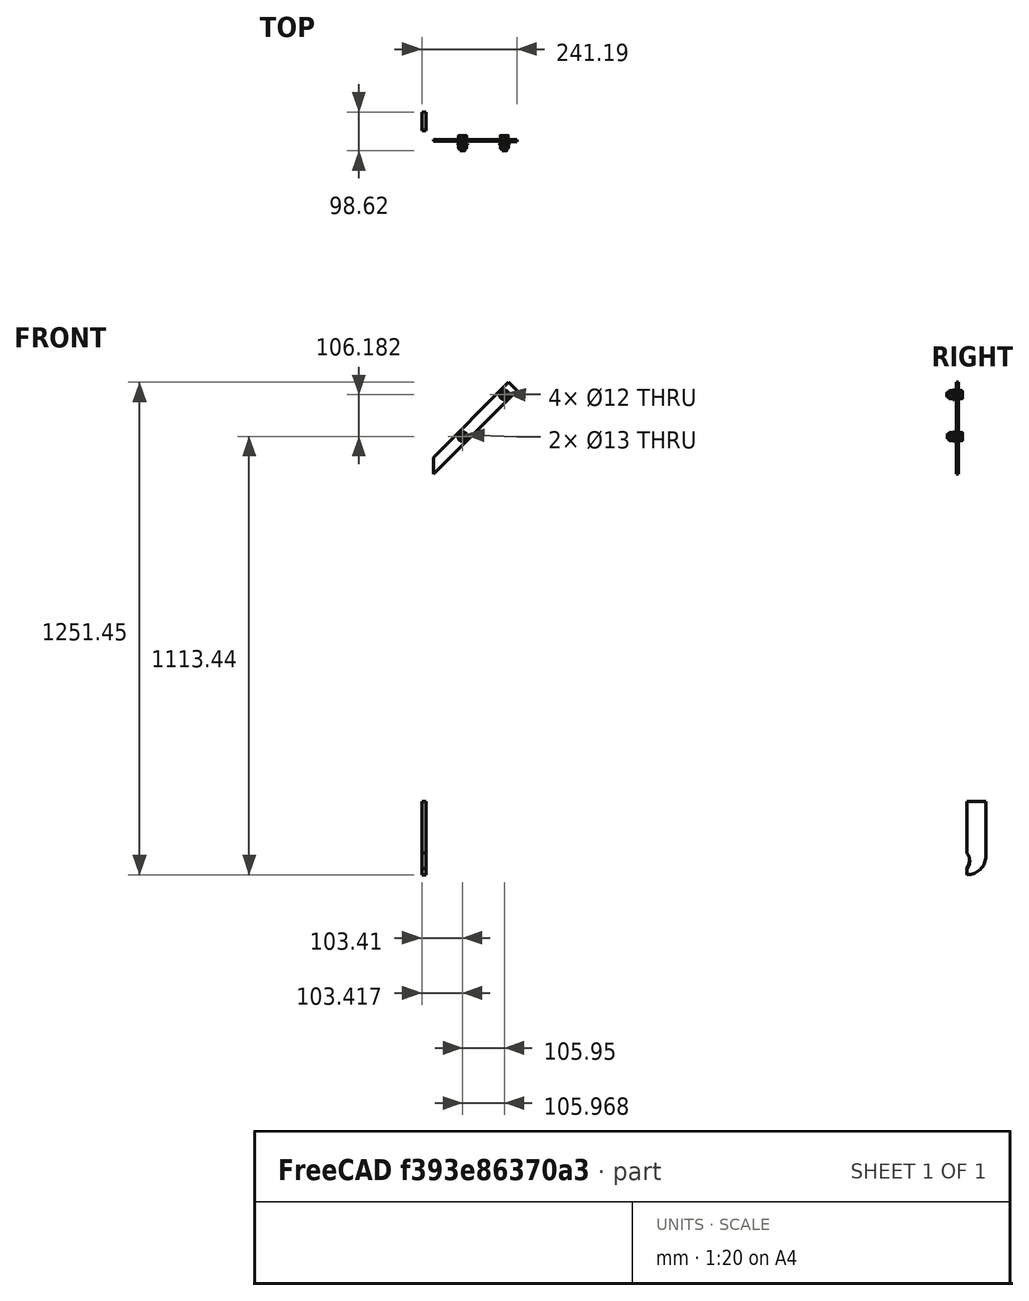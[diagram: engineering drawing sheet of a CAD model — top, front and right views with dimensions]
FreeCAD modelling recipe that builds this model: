
FCSTD DOCUMENT  (FreeCAD 0.20R29177 (Git))
Label: Tail_Assembly_BoomVane
License: All rights reserved
LicenseURL: http://en.wikipedia.org/wiki/All_rights_reserved
objects: App::Link×5, Spreadsheet::Sheet×1, Part::Mirroring×1, Part::Cylinder×1, Part::Cut×1, App::Part×1
note: 3 computed .brp shape members not serialized (recipe doc carries the construction recipe); baked Part::Feature solids carry a one-line shape summary decoded from their .brp
EXTERNAL_REF file=Boom/Tail_Boom_Support.FCStd obj=PadBody
EXTERNAL_REF file=../Master_of_Puppets.FCStd obj=HighEndStop
EXTERNAL_REF file=../Master_of_Puppets.FCStd obj=Spreadsheet
EXTERNAL_REF file=../Master_of_Puppets.FCStd obj=Tail
EXTERNAL_REF file=Vane/Tail_Vane_Bracket.FCStd obj=Part
EXTERNAL_REF file=Boom/Tail_Boom_Pipe.FCStd obj=Tube
EXTERNAL_REF file=Vane/Tail_Vane.FCStd obj=Fillet001Body
EXTERNAL_REF file=Stops/Tail_Stop_HighEnd.FCStd obj=PadBody

FEATURE [App::Link] Link001  label="Boom_Support"
  LinkPlacement = pos=(24.15,0,0) rot=(0,0,1;0.087712rad)
  LinkTransform = true
  LinkedObject = -> <external Boom/Tail_Boom_Support.FCStd>#PadBody
  Placement = pos=(24.15,0,0) rot=(0,0,1;0.087712rad)
  expr: .LinkPlacement.Base.x = Spreadsheet.TailBoomTriangularBraceX
  expr: .LinkPlacement.Base.y = Spreadsheet.TailBoomTriangularBraceY
  expr: .LinkPlacement.Base.z = Spreadsheet.TailBoomTriangularBraceZ
  expr: .LinkPlacement.Rotation.Angle = Spreadsheet.TailBoomTriangularBraceZAxisAngle
FEATURE [Spreadsheet::Sheet] Spreadsheet
  cells = A1=Inputs; A2=BoomPipeDiameter; B2(BoomPipeDiameter)==Master_of_Puppets#Spreadsheet.BoomPipeDiameter; A3=FlatMetalThickness; B3(FlatMetalThickness)==Master_of_Puppets#Spreadsheet.FlatMetalThickness; A4=BracketThickness; B4(BracketThickness)==Master_of_Puppets#Spreadsheet.BracketThickness; A5=BoomLength; B5(BoomLength)==Master_of_Puppets#Spreadsheet.BoomLength; A6=BracketLength; B6(BracketLength)==Master_of_Puppets#Spreadsheet.BracketLength; A7=BracketWidth; B7(BracketWidth)==Master_of_Puppets#Spreadsheet.BracketWidth; A8=VerticalPlaneAngle; B8(VerticalPlaneAngle)==Master_of_Puppets#Spreadsheet.VerticalPlaneAngle; A9=VaneBracketAngle; B9(VaneBracketAngle)==Master_of_Puppets#Tail.VaneBracketAngle; A10=TailBoomTriangularBraceZAxisAngle; B10(TailBoomTriangularBraceZAxisAngle)==Master_of_Puppets#Tail.TailBoomTriangularBraceZAxisAngle; A11=VaneThickness; B11(VaneThickness)==Master_of_Puppets#Spreadsheet.VaneThickness; A12=HingeOuterPipeRadius; B12(HingeOuterPipeRadius)==Master_of_Puppets#Tail.HingeOuterPipeRadius; A13=HingeOuterPipeLength; B13(HingeOuterPipeLength)==Master_of_Puppets#Tail.HingeOuterPipeLength; A14=OuterTailHingePlacement; B14(OuterTailHingePlacement)==Master_of_Puppets#Tail.OuterTailHingePlacement; A15=TailPlacement (TailBoomVaneAssembly); B15(TailPlacement)==Master_of_Puppets#HighEndStop.TailPlacement; A16=Calculated; A17=BoomPipeRadius; B17(BoomPipeRadius)==BoomPipeDiameter / 2; A18=Placement; A19=TailAssemblyBoomVane; B19=HighEndStopPlacement; A20(TailAssemblyBoomVanePlacement)==create(<<placement>>; create(<<vector>>); create(<<rotation>>; create(<<vector>>; 0; 1; 0); 90)); B20(HighEndStopPlacement)==Master_of_Puppets#HighEndStop.HighEndStopPlacement; A21=TailBoomTriangularBrace; A22=X; B22=Y; C22=Z; A23(TailBoomTriangularBraceX)==BoomPipeRadius; B23(TailBoomTriangularBraceY)=0; C23(TailBoomTriangularBraceZ)=0; A24=TopTailVaneBracket; A25=BracketWidthTriangleSide; B25=TailVaneBracketXOffset; C25=BracketLengthTriangleSide; A26(BracketWidthTriangleSide)==BracketWidth * cos(VaneBracketAngle); B26(TailVaneBracketXOffset)==BoomPipeRadius + BracketWidthTriangleSide; C26(BracketLengthTriangleSide)==BracketLength * cos(VaneBracketAngle); A27=Opposite; B27=BracketEndAdajcent; C27=BracketHypotenuse; A28(Opposite)==sin(VaneBracketAngle) * BracketLength; B28(BracketEndAdajcent)==cos(90 - VaneBracketAngle) * BracketWidth; C28(BracketHypotenuse)==BracketWidth / sin(VaneBracketAngle); A29=X; B29=Y; C29=Z; A30(TopTailVaneBracketX)==(Opposite + 2 * BoomPipeRadius - TailVaneBracketXOffset) * -1; B30(TopTailVaneBracketY)==-BracketThickness / 2; C30(TopTailVaneBracketZ)==BoomLength + BracketLengthTriangleSide + BracketEndAdajcent - BracketHypotenuse; B31=TopTailVaneBracketY Duplicated in Tail; A32=Angle; A33(TopTailVaneBracketAngle)==-VaneBracketAngle; A34=TailVane; A35=X; B35=Y; C35=Z; A36(TailVaneX)=0; B36(TailVaneY)==TopTailVaneBracketY - VaneThickness; C36(TailVaneZ)==BoomLength; A37=HingeOuterCylinder; A38(HingeOuterCylinderPlacement)==minvert(TailAssemblyBoomVanePlacement) * minvert(TailPlacement) * OuterTailHingePlacement
FEATURE [App::Link] Link004  label="Vane_Bracket_Top"
  LinkPlacement = pos=(-215.069,-2.5,1190.92) rot=(0,1,0;-0.785398rad)
  LinkTransform = true
  LinkedObject = -> <external Vane/Tail_Vane_Bracket.FCStd>#Part
  Placement = pos=(-215.069,-2.5,1190.92) rot=(0,1,0;-0.785398rad)
  expr: .LinkPlacement.Base.x = Spreadsheet.TopTailVaneBracketX
  expr: .LinkPlacement.Base.y = Spreadsheet.TopTailVaneBracketY
  expr: .LinkPlacement.Base.z = Spreadsheet.TopTailVaneBracketZ
  expr: .LinkPlacement.Rotation.Angle = Spreadsheet.TopTailVaneBracketAngle
FEATURE [App::Link] Link  label="Boom_Pipe"
  LinkedObject = -> <external Boom/Tail_Boom_Pipe.FCStd>#Tube
FEATURE [Part::Mirroring] mirror  label="Vane_Bracket_Bottom"
  Base = (0.000366211,-6.84779,1074.31)
  Normal = (1,-0.000576858,0.000545144)
  Source = -> Link004
FEATURE [App::Link] Link005  label="Vane"
  LinkPlacement = pos=(0,-8.5,1000) rot=(-0.57735,-0.57735,-0.57735;2.0944rad)
  LinkedObject = -> <external Vane/Tail_Vane.FCStd>#Fillet001Body
  Placement = pos=(0,-8.5,1000) rot=(-0.57735,-0.57735,-0.57735;2.0944rad)
  expr: .Placement.Base.x = Spreadsheet.TailVaneX
  expr: .Placement.Base.y = Spreadsheet.TailVaneY
  expr: .Placement.Base.z = Spreadsheet.TailVaneZ
FEATURE [Part::Cylinder] Cylinder  label="Hinge_Outer_Cylinder"
  Angle = 360
  AttacherType = Attacher::AttachEngine3D
  FirstAngle = 0
  Height = 126.076
  Placement = pos=(74.8689,7.40405,-49.5225) rot=(0.183254,-0.974655,-0.128316;1.24596rad)
  Radius = 30.15
  SecondAngle = 0
  expr: Height = Spreadsheet.HingeOuterPipeLength
  expr: Placement = Spreadsheet.HingeOuterCylinderPlacement
  expr: Radius = Spreadsheet.HingeOuterPipeRadius
FEATURE [App::Link] Link002  label="Stop_HighEnd_Link"
  LinkPlacement = pos=(5,24.15,0) rot=(0,1,0;-1.5708rad)
  LinkedObject = -> <external Stops/Tail_Stop_HighEnd.FCStd>#PadBody
  Placement = pos=(5,24.15,0) rot=(0,1,0;-1.5708rad)
  expr: Placement = Spreadsheet.HighEndStopPlacement
FEATURE [Part::Cut] Cut  label="Tail_Stop_HighEnd"
  Base = -> Link002
  Openafpm_Flat = true
  Tool = -> Cylinder
FEATURE [App::Part] Part001  label="Tail_Assembly_BoomVane"
  Group = -> [Link,Link001,Link004,mirror,Link005,Link002,Cylinder,Cut]
  Origin = -> Origin001
  Placement = pos=(0,0,0) rot=(0,1,0;1.5708rad)

RESOLVED EXTERNAL PARTS (link-assembly join: the EXTERNAL_REF files above that resolve inside this repo's crawl, each included once):
---- part ../Master_of_Puppets.FCStd = doc fcstd_6404554055c4 (61625 chars; too large to inline — full recipe in that document) ----
---- part Boom/Tail_Boom_Support.FCStd = doc fcstd_6b65ddd8a587 ----
FCSTD DOCUMENT  (FreeCAD 0.19R24366 (Git))
Label: Tail_Boom_Support
License: All rights reserved
LicenseURL: http://en.wikipedia.org/wiki/All_rights_reserved
objects: Sketcher::SketchObject×1, PartDesign::Pad×1, Spreadsheet::Sheet×1, PartDesign::Body×1
note: 4 computed .brp shape members not serialized (recipe doc carries the construction recipe); baked Part::Feature solids carry a one-line shape summary decoded from their .brp
EXTERNAL_REF file=../../Master_of_Puppets.FCStd obj=Spreadsheet
EXTERNAL_REF file=../../Master_of_Puppets.FCStd obj=Tail

FEATURE [Sketcher::SketchObject] Sketch
  FullyConstrained = true
  MapMode = 5
  Support = -> [XY_Plane001]
  expr: Constraints[17] = Spreadsheet.SupportLength
  expr: Constraints[2] = Spreadsheet.TailBoomTriangularBraceLength
  expr: Constraints[16] = Spreadsheet.SupportWidth
  expr: Constraints[7] = Spreadsheet.TriangularAngle
  expr: Constraints[4] = Spreadsheet.TailBoomTriangularBraceWidth
  sketch-geometry (7):
    g0: LineSegment StartX=333.333 StartY=0 StartZ=0 EndX=-26.8829 EndY=-73.86 EndZ=0
    g1: LineSegment StartX=0 StartY=0 StartZ=0 EndX=333.333 EndY=0 EndZ=0
    g2: LineSegment StartX=-26.8829 StartY=-73.86 StartZ=0 EndX=0 EndY=0 EndZ=0
    g3: LineSegment StartX=-26.8829 StartY=-73.86 StartZ=0 EndX=333.333 EndY=0 EndZ=0
    g4: LineSegment StartX=-26.8829 StartY=-73.86 StartZ=0 EndX=1.14859e-11 EndY=1.64988e-11 EndZ=0
    g5: LineSegment StartX=1.14859e-11 StartY=1.64988e-11 StartZ=0 EndX=1.6e-14 EndY=0 EndZ=0
    g6: LineSegment StartX=1.6e-14 StartY=0 StartZ=0 EndX=333.333 EndY=0 EndZ=0
  constraints (18):
    c: PointOnObject(g0,g-1)
    c: Coincident(g0,g1)
    c: Distance(g1,g0) = 333.333
    c: Coincident(g2,g0)
    c: Distance(g2,g0) = 78.6002
    c: Coincident(g1,g2)
    c: Coincident(g1,g-1)
    c: Angle(g2,g1) = 1.91986
    c: Coincident(g3,g0)
    c: Coincident(g3,g0)
    c: Coincident(g4,g3)
    c: PointOnObject(g4,g2)
    c: Coincident(g5,g4)
    c: PointOnObject(g5,g1)
    c: Coincident(g6,g5)
    c: Coincident(g6,g3)
    c: Distance(g4,g3) = 78.6002
    c: Distance(g5,g3) = 333.333
FEATURE [PartDesign::Pad] Pad
  AllowMultiFace = false
  Direction = (1,1,1)
  Length = 10
  Length2 = 100
  Profile = -> Sketch
  Type = 0
  expr: Length = Spreadsheet.FlatMetalThickness
FEATURE [Spreadsheet::Sheet] Spreadsheet
  cells = A1=Inputs; A2=CalculatedWindTurbineShape; B2(CalculatedWindTurbineShape)==Master_of_Puppets#Spreadsheet.CalculatedWindTurbineShape; D2=a; E2(a)==TailBoomTriangularBraceWidth; A3=VerticalPlaneAngle; B3(VerticalPlaneAngle)==Master_of_Puppets#Spreadsheet.VerticalPlaneAngle; D3=b; E3(b)==TailBoomTriangularBraceLength; A4=FlatMetalThickness; B4(FlatMetalThickness)==Master_of_Puppets#Spreadsheet.FlatMetalThickness; D4=c; E4(c)==sqrt(a ^ 2 + b ^ 2 - 2 * a * b * cos(TriangularAngle)); F4=Law of Cosines; A5=TailBoomTriangularBraceWidth; B5(TailBoomTriangularBraceWidth)==Master_of_Puppets#Tail.TailBoomTriangularBraceWidth; D5=AngleA; E5(AngleA)==acos((a ^ 2 + c ^ 2 - b ^ 2) / (2 * a * c)); F5=Law of Cosines; A6=TailBoomTriangularBraceLength; B6(TailBoomTriangularBraceLength)==Master_of_Puppets#Tail.TailBoomTriangularBraceLength; D6=AngleB; E6(AngleB)==acos((b ^ 2 + c ^ 2 - a ^ 2) / (2 * b * c)); F6=Law of Cosines; A7=Calculated; D7=WidthOfFlatBar; E7(WidthOfFlatBar)=100; A8=TriangularAngle; B8(TriangularAngle)==90 + VerticalPlaneAngle; D8=x; E8(x)==WidthOfFlatBar / sin(AngleB); A9=Y; B9(Y)==FlatMetalThickness / 2; D9=y; E9(y)==WidthOfFlatBar / sin(AngleA); A10=SupportWidth; B10(SupportWidth)==CalculatedWindTurbineShape == <<T>> ? TailBoomTriangularBraceWidth : y; A11=SupportLength; B11(SupportLength)==CalculatedWindTurbineShape == <<T>> ? TailBoomTriangularBraceLength : x
FEATURE [PartDesign::Body] PadBody  label="Tail_Boom_Support"
  Group = -> [Sketch,Pad]
  Openafpm_Flat = true
  Origin = -> Origin001
  Placement = pos=(0,5,0) rot=(0.57735,-0.57735,0.57735;2.0944rad)
  Tip = -> Pad
  expr: .Placement.Base.y = Spreadsheet.Y
---- part Stops/Tail_Stop_HighEnd.FCStd = doc fcstd_737cbc09fbdb ----
FCSTD DOCUMENT  (FreeCAD 0.21R33771 (Git))
Label: Tail_Stop_HighEnd
License: All rights reserved
LicenseURL: http://en.wikipedia.org/wiki/All_rights_reserved
objects: Sketcher::SketchObject×1, PartDesign::Pad×1, Spreadsheet::Sheet×1, PartDesign::Body×1
note: 4 computed .brp shape members not serialized (recipe doc carries the construction recipe); baked Part::Feature solids carry a one-line shape summary decoded from their .brp
EXTERNAL_REF file=../../Master_of_Puppets.FCStd obj=HighEndStop
EXTERNAL_REF file=../../Master_of_Puppets.FCStd obj=Spreadsheet
EXTERNAL_REF file=../../Master_of_Puppets.FCStd obj=Tail

FEATURE [Sketcher::SketchObject] Sketch
  FullyConstrained = true
  MapMode = 5
  Support = -> [XY_Plane001]
  expr: Constraints[14] = Spreadsheet.HingeOuterPipeRadius
  expr: Constraints[16] = Spreadsheet.HingeOuterPipeDiameter
  expr: Constraints[1] = Spreadsheet.HighEndStopWidth
  expr: Constraints[3] = Spreadsheet.HighEndStopLength
  expr: Constraints[8] = Spreadsheet.HighEndStopWidthExtensionToLowEndStop
  sketch-geometry (7):
    g0: LineSegment StartX=223.325 StartY=0 StartZ=0 EndX=223.325 EndY=118.216 EndZ=0
    g1: ArcOfCircle CenterX=16.6164 CenterY=0 CenterZ=0 NormalX=0 NormalY=0 NormalZ=1 AngleXU=0 Radius=118.216 StartAngle=1.5708 EndAngle=3.14159
    g2: LineSegment StartX=16.6164 StartY=118.216 StartZ=0 EndX=223.325 EndY=118.216 EndZ=0
    g3: LineSegment StartX=-101.6 StartY=1.45e-14 StartZ=0 EndX=-101.6 EndY=-4.64258 EndZ=0
    g4: LineSegment StartX=-101.6 StartY=-4.64258 StartZ=0 EndX=-50.8 EndY=-4.64258 EndZ=0
    g5: LineSegment StartX=-50.8 StartY=-4.64258 StartZ=0 EndX=-50.8 EndY=0 EndZ=0
    g6: LineSegment StartX=223.325 StartY=0 StartZ=0 EndX=-50.8 EndY=0 EndZ=0
  constraints (22):
    c: Vertical(g0)
    c: DistanceY(g0,g0) = 118.216
    c: PointOnObject(g1,g-1)
    c: DistanceX(g-1,g0) = 223.325
    c: Coincident(g2,g1)
    c: Coincident(g2,g0)
    c: Vertical(g3)
    c: Coincident(g3,g4)
    c: DistanceY(g4,g1) = 4.64258
    c: Coincident(g3,g1)
    c: Horizontal(g2)
    c: Coincident(g5,g4)
    c: PointOnObject(g5,g-1)
    c: Vertical(g5)
    c: DistanceX(g4,g4) = 50.8
    c: Horizontal(g4)
    c: DistanceX(g1,g-1) = 101.6
    c: Vertical(g1,g1)
    c: Coincident(g6,g0)
    c: Coincident(g6,g5)
    c: Horizontal(g6)
    c: PointOnObject(g1,g6)
FEATURE [PartDesign::Pad] Pad
  AllowMultiFace = false
  Direction = (0,0,1)
  Length = 10
  Length2 = 100
  Profile = -> Sketch
  Type = 0
  expr: Length = Spreadsheet.FlatMetalThickness
FEATURE [Spreadsheet::Sheet] Spreadsheet
  cells = A1='Inputs; A2='FlatMetalThickness; B2(FlatMetalThickness)==Master_of_Puppets#Spreadsheet.FlatMetalThickness; A3='HingeOuterPipeRadius; B3(HingeOuterPipeRadius)==Master_of_Puppets#Tail.HingeOuterPipeRadius; A4='HighEndStopWidth; B4(HighEndStopWidth)==Master_of_Puppets#HighEndStop.HighEndStopWidth; A5='HighEndStopLength; B5(HighEndStopLength)==Master_of_Puppets#HighEndStop.HighEndStopLength; A6='HighEndStopWidthExtensionToLowEndStop; B6(HighEndStopWidthExtensionToLowEndStop)==Master_of_Puppets#HighEndStop.HighEndStopWidthExtensionToLowEndStop; A7='Calculated; A8='HingeOuterPipeDiameter; B8(HingeOuterPipeDiameter)==HingeOuterPipeRadius * 2; C8='Distance stop extends towards the outer tail hinge
FEATURE [PartDesign::Body] PadBody  label="Tail_Stop_HighEnd"
  Group = -> [Sketch,Pad]
  Origin = -> Origin001
  Tip = -> Pad
---- part Vane/Tail_Vane.FCStd = doc fcstd_911bd00fbed7 ----
FCSTD DOCUMENT  (FreeCAD 1.0R39109 (Git))
Label: Tail_Vane
License: All rights reserved
LicenseURL: http://en.wikipedia.org/wiki/All_rights_reserved
objects: Sketcher::SketchObject×2, PartDesign::Pad×1, Spreadsheet::Sheet×1, PartDesign::Plane×1, PartDesign::Pocket×1, PartDesign::Mirrored×1, PartDesign::Fillet×1, PartDesign::Body×1
note: 17 computed .brp shape members not serialized (recipe doc carries the construction recipe); baked Part::Feature solids carry a one-line shape summary decoded from their .brp
EXTERNAL_REF file=../../Master_of_Puppets.FCStd obj=Alternator
EXTERNAL_REF file=../../Master_of_Puppets.FCStd obj=Spreadsheet
EXTERNAL_REF file=../../Master_of_Puppets.FCStd obj=Tail

FEATURE [Sketcher::SketchObject] Sketch
  ArcFitTolerance = 0
  AttachmentSupport = -> [XY_Plane001]
  FullyConstrained = true
  MakeInternals = false
  MapMode = 5
  expr: Constraints[16] = Spreadsheet.VaneWidth
  expr: Constraints[17] = Spreadsheet.VaneLength
  expr: Constraints[18] = Spreadsheet.LengthSmallSide
  expr: Constraints[19] = Spreadsheet.WidthSmall
  sketch-geometry (7):
    g0: LineSegment StartX=0 StartY=94.8607 StartZ=0 EndX=0 EndY=0 EndZ=0
    g1: LineSegment StartX=0 StartY=0 StartZ=0 EndX=0 EndY=-94.8607 EndZ=0
    g2: LineSegment StartX=0 StartY=-94.8607 StartZ=0 EndX=427.594 EndY=-1000 EndZ=0
    g3: LineSegment StartX=427.594 StartY=-1000 StartZ=0 EndX=900 EndY=-1000 EndZ=0
    g4: LineSegment StartX=900 StartY=-1000 StartZ=0 EndX=900 EndY=1000 EndZ=0
    g5: LineSegment StartX=900 StartY=1000 StartZ=0 EndX=427.594 EndY=1000 EndZ=0
    g6: LineSegment StartX=427.594 StartY=1000 StartZ=0 EndX=0 EndY=94.8607 EndZ=0
  constraints (20):
    c: PointOnObject(g0,g-2)
    c: Coincident(g0,g-1)
    c: Coincident(g-1,g1)
    c: PointOnObject(g1,g-2)
    c: Coincident(g1,g2)
    c: Coincident(g2,g3)
    c: Horizontal(g3)
    c: Coincident(g3,g4)
    c: Vertical(g4)
    c: Coincident(g4,g5)
    c: Horizontal(g5)
    c: Coincident(g5,g6)
    c: Coincident(g6,g0)
    c: Equal(g6,g2)
    c: Equal(g5,g3)
    c: Equal(g0,g1)
    c: DistanceX(g-1,g4) = 900
    c: DistanceY(g4,g4) = 2000
    c: DistanceY(g1,g1) = 94.8607
    c: DistanceX(g5,g5) = 472.406
FEATURE [PartDesign::Pad] Pad
  AllowMultiFace = false
  Direction = (0,0,1)
  Length = 9
  Length2 = 100
  Profile = -> Sketch
  Suppressed = false
  Type = 0
  expr: Length = Spreadsheet.VaneThickness
FEATURE [Spreadsheet::Sheet] Spreadsheet
  cells = A1='Inputs; A2='RotorRadius; B2(RotorRadius)==Master_of_Puppets#Spreadsheet.RotorDiskRadius; A3='BoomPipeDiameter; B3(BoomPipeDiameter)==Master_of_Puppets#Spreadsheet.BoomPipeDiameter; A4='HolesRadius; B4(HolesRadius)==Master_of_Puppets#Alternator.HolesRadius; A5='BracketLength; B5(BracketLength)==Master_of_Puppets#Spreadsheet.BracketLength; A6='BracketWidth; B6(BracketWidth)==Master_of_Puppets#Spreadsheet.BracketWidth; A7='VaneLength; B7(VaneLength)==Master_of_Puppets#Spreadsheet.VaneLength; A8='VaneWidth; B8(VaneWidth)==Master_of_Puppets#Spreadsheet.VaneWidth; A9='VaneThickness; B9(VaneThickness)==Master_of_Puppets#Spreadsheet.VaneThickness; A10='DistanceToFirstHole; B10(DistanceToFirstHole)==Master_of_Puppets#Tail.DistanceToFirstHole; A11='DistanceBetweenHoles; B11(DistanceBetweenHoles)==Master_of_Puppets#Tail.DistanceBetweenHoles; A12='VaneBracketAngle; B12(VaneBracketAngle)==Master_of_Puppets#Tail.VaneBracketAngle; A13='Calculated; A14='BoomPipeRadius; B14(BoomPipeRadius)==BoomPipeDiameter / 2; A15='Y_Holes; B15(Y_Holes)==BracketWidth / 2; C15='Duplicated in TailVaneBracket; A16='WidthAngleBracket; B16(WidthAngleBracket)==BracketWidth / cos(VaneBracketAngle); A17='HalfWidthAngleBracket; B17(HalfWidthAngleBracket)==WidthAngleBracket / 2; A18='LengthSmallSide; B18(LengthSmallSide)==tan(VaneBracketAngle) * WidthAngleBracket + BoomPipeRadius; A19='WidthSmall; B19(WidthSmall)==0.5 * VaneWidth / (1 - LengthSmallSide / VaneLength); A20='DistanceToFirstHoleFromMiddlePoint; B20(DistanceToFirstHoleFromMiddlePoint)==BracketLength - Y_Holes - DistanceToFirstHole
FEATURE [PartDesign::Plane] DatumPlane
  Length = 60
  MapMode = 2
  Placement = pos=(0,0,9) rot=(0,0,1;0rad)
  ResizeMode = 0
  Width = 60
  expr: .Placement.Base.z = Spreadsheet.VaneThickness
FEATURE [Sketcher::SketchObject] Sketch001  label="HolesSketch"
  ArcFitTolerance = 0
  AttachmentSupport = -> [DatumPlane]
  FullyConstrained = true
  MakeInternals = false
  MapMode = 5
  Placement = pos=(0,0,9) rot=(0,0,1;0rad)
  expr: Constraints[0] = Spreadsheet.BoomPipeRadius
  expr: Constraints[11] = Spreadsheet.BracketLength
  expr: Constraints[13] = Spreadsheet.DistanceToFirstHoleFromMiddlePoint
  expr: Constraints[18] = Spreadsheet.WidthAngleBracket / 2
  expr: Constraints[2] = Spreadsheet.Y_Holes
  expr: Constraints[4] = Spreadsheet.DistanceBetweenHoles
  expr: Constraints[6] = Spreadsheet.HolesRadius
  expr: Constraints[7] = Spreadsheet.HolesRadius
  expr: Constraints[8] = Spreadsheet.WidthAngleBracket
  sketch-geometry (7):
    g0: LineSegment [constr] StartX=353.553 StartY=-448.414 StartZ=0 EndX=388.909 EndY=-413.059 EndZ=0
    g1: LineSegment [constr] StartX=371.231 StartY=-430.736 StartZ=0 EndX=-35.3553 EndY=-24.15 EndZ=0
    g2: Circle CenterX=328.805 CenterY=-388.31 CenterZ=0 NormalX=0 NormalY=0 NormalZ=1 AngleXU=0 Radius=7
    g3: Circle CenterX=116.673 CenterY=-176.178 CenterZ=0 NormalX=0 NormalY=0 NormalZ=1 AngleXU=0 Radius=7
    g4: LineSegment [constr] StartX=388.909 StartY=-413.059 StartZ=0 EndX=0 EndY=-24.15 EndZ=0
    g5: LineSegment [constr] StartX=353.553 StartY=-448.414 StartZ=0 EndX=-70.7107 EndY=-24.15 EndZ=0
    g6: LineSegment [constr] StartX=-70.7107 StartY=-24.15 StartZ=0 EndX=0 EndY=-24.15 EndZ=0
  constraints (22):
    c: DistanceY(g4,g-1) = 24.15
    c: PointOnObject(g1,g0)
    c: Distance(g1,g0) = 25
    c: PointOnObject(g3,g1)
    c: Distance(g2,g3) = 300
    c: Angle(g1) = 2.35619
    c: Radius(g3) = 7
    c: Radius(g2) = 7
    c: Distance(g6,g4) = 70.7107
    c: Coincident(g4,g0)
    c: Coincident(g5,g0)
    c: Distance(g6,g0) = 600
    c: PointOnObject(g2,g1)
    c: Distance(g2,g1) = 515
    c: Perpendicular(g0,g1)
    c: PointOnObject(g4,g-2)
    c: Horizontal(g6)
    c: PointOnObject(g1,g6)
    c: Distance(g4,g1) = 35.3553
    c: Coincident(g5,g6)
    c: Coincident(g4,g6)
    c: Perpendicular(g5,g0)
FEATURE [PartDesign::Pocket] Pocket
  BaseFeature = -> Pad
  Direction = (0,0,-1)
  Length = 9
  Length2 = 100
  Profile = -> Sketch001
  Suppressed = false
  Type = 0
  expr: Length = Spreadsheet.VaneThickness
FEATURE [PartDesign::Mirrored] Mirrored
  BaseFeature = -> Pocket
  MirrorPlane = -> Sketch001 [H_Axis]
  Originals = -> [Pocket]
  Suppressed = false
  TransformMode = 0
FEATURE [PartDesign::Fillet] Fillet
  Base = -> Mirrored [Edge1,Edge8,Edge28,Edge29,Edge27,Edge5]
  BaseFeature = -> Mirrored
  Radius = 50
  SupportTransform = false
  Suppressed = false
  UseAllEdges = false
FEATURE [PartDesign::Body] Fillet001Body  label="Tail_Vane"
  AllowCompound = false
  Group = -> [Sketch,Pad,DatumPlane,Sketch001,Pocket,Mirrored,Fillet]
  Openafpm_Flat = true
  Origin = -> Origin001
  Placement = pos=(0,0,8) rot=(0,0,1;0rad)
  Tip = -> Fillet
---- part Vane/Tail_Vane_Bracket.FCStd = doc fcstd_d393650c2bc9 ----
FCSTD DOCUMENT  (FreeCAD 0.21R33771 (Git))
Label: Tail_Vane_Bracket
License: All rights reserved
LicenseURL: http://en.wikipedia.org/wiki/All_rights_reserved
objects: App::Link×4, Sketcher::SketchObject×2, App::Part×2, PartDesign::Pad×1, PartDesign::Pocket×1, Spreadsheet::Sheet×1, PartDesign::Body×1
note: 7 computed .brp shape members not serialized (recipe doc carries the construction recipe); baked Part::Feature solids carry a one-line shape summary decoded from their .brp
EXTERNAL_REF file=../../Master_of_Puppets.FCStd obj=Alternator
EXTERNAL_REF file=../../Master_of_Puppets.FCStd obj=Fastener
EXTERNAL_REF file=../../Master_of_Puppets.FCStd obj=Spreadsheet
EXTERNAL_REF file=../../Master_of_Puppets.FCStd obj=Tail
EXTERNAL_REF file=../../Fasteners/Fastener_Bolt_Tail_Vane.FCStd obj=Body
EXTERNAL_REF file=../../Fasteners/Fastener_HexNut.FCStd obj=Body
EXTERNAL_REF file=../../Fasteners/Fastener_Washer_Wide.FCStd obj=Tube

FEATURE [Sketcher::SketchObject] Sketch
  FullyConstrained = true
  MapMode = 5
  Support = -> [XY_Plane001]
  expr: Constraints[10] = Spreadsheet.Length
  expr: Constraints[7] = Spreadsheet.VaneBracketAngle
  expr: Constraints[8] = Spreadsheet.Width
  sketch-geometry (4):
    g0: LineSegment StartX=300 StartY=30 StartZ=0 EndX=0 EndY=30 EndZ=0
    g1: LineSegment StartX=0 StartY=30 StartZ=0 EndX=0 EndY=0 EndZ=0
    g2: LineSegment StartX=0 StartY=0 StartZ=0 EndX=270 EndY=0 EndZ=0
    g3: LineSegment StartX=270 StartY=0 StartZ=0 EndX=300 EndY=30 EndZ=0
  constraints (11):
    c: Coincident(g0,g1)
    c: Horizontal(g0)
    c: Vertical(g1)
    c: Coincident(g-1,g2)
    c: Horizontal(g2)
    c: Coincident(g2,g3)
    c: Coincident(g3,g0)
    c: Angle(g0,g3) = 0.785398
    c: DistanceY(g1,g1) = 30
    c: Coincident(g1,g-1)
    c: Distance(g0) = 300
FEATURE [PartDesign::Pad] Pad
  AllowMultiFace = false
  Direction = (0,0,1)
  Length = 5
  Length2 = 100
  Profile = -> Sketch
  Type = 0
  expr: Length = Spreadsheet.BracketThickness
FEATURE [Sketcher::SketchObject] Sketch001
  FullyConstrained = true
  MapMode = 5
  Placement = pos=(0,0,5) rot=(0,0,1;0rad)
  Support = -> [Pad]
  expr: Constraints[10] = Spreadsheet.DistanceBetweenHoles
  expr: Constraints[7] = Spreadsheet.Y_Holes
  expr: Constraints[8] = Spreadsheet.HolesRadius
  expr: Constraints[9] = Spreadsheet.DistanceToFirstHole
  sketch-geometry (4):
    g0: Circle CenterX=30 CenterY=15 CenterZ=0 NormalX=0 NormalY=0 NormalZ=1 AngleXU=0 Radius=6
    g1: Circle CenterX=180 CenterY=15 CenterZ=0 NormalX=0 NormalY=0 NormalZ=1 AngleXU=0 Radius=6
    g2: LineSegment StartX=0 StartY=15 StartZ=0 EndX=30 EndY=15 EndZ=0
    g3: LineSegment StartX=30 StartY=15 StartZ=0 EndX=180 EndY=15 EndZ=0
  constraints (11):
    c: Equal(g1,g0)
    c: PointOnObject(g2,g-2)
    c: Coincident(g2,g0)
    c: Horizontal(g2)
    c: Coincident(g2,g3)
    c: Coincident(g3,g1)
    c: Horizontal(g3)
    c: Distance(g-1,g2) = 15
    c: Radius(g0) = 6
    c: DistanceX(g2,g2) = 30
    c: DistanceX(g3,g3) = 150
FEATURE [PartDesign::Pocket] Pocket
  AllowMultiFace = false
  BaseFeature = -> Pad
  Direction = (0,0,-1)
  Length = 5
  Length2 = 100
  Profile = -> Sketch001
  Type = 1
FEATURE [Spreadsheet::Sheet] Spreadsheet
  cells = A1='Inputs; A2='Width; B2(Width)==Master_of_Puppets#Spreadsheet.BracketWidth; A3='Length; B3(Length)==Master_of_Puppets#Spreadsheet.BracketLength; A4='BracketThickness; B4(BracketThickness)==Master_of_Puppets#Spreadsheet.BracketThickness; A5='HolesRadius; B5(HolesRadius)==Master_of_Puppets#Alternator.HolesRadius; A6='DistanceToFirstHole; B6(DistanceToFirstHole)==Master_of_Puppets#Tail.DistanceToFirstHole; A7='DistanceBetweenHoles; B7(DistanceBetweenHoles)==Master_of_Puppets#Tail.DistanceBetweenHoles; A8='VaneBracketAngle; B8(VaneBracketAngle)==Master_of_Puppets#Tail.VaneBracketAngle; A9='VaneThickness; B9(VaneThickness)==Master_of_Puppets#Spreadsheet.VaneThickness; A10='FlatMetalThickness; B10(FlatMetalThickness)==Master_of_Puppets#Spreadsheet.FlatMetalThickness; A11='HexNutThickness; B11(HexNutThickness)==Master_of_Puppets#Fastener.HexNutThickness; A12='WasherThickness; B12(WasherThickness)==Master_of_Puppets#Fastener.WasherThickness; A13='TailVaneBracketBoltLength; B13(TailVaneBracketBoltLength)==Master_of_Puppets#Fastener.TailVaneBracketBoltLength; A14='DistanceThreadsExtendFromNuts; B14(DistanceThreadsExtendFromNuts)==Master_of_Puppets#Fastener.DistanceThreadsExtendFromNuts; A15='Placement; A16='Y_Holes; B16(Y_Holes)==Width / 2; C16='Duplicated in TailVane; A17='BoltZ; B17(BoltZ)==BracketThickness; A18='DistanceToSecondHole; B18(DistanceToSecondHole)==DistanceToFirstHole + DistanceBetweenHoles; A19='WasherZ; B19(WasherZ)==-WasherThickness - VaneThickness; A20='HexNutZ; B20(HexNutZ)==-HexNutThickness + WasherZ
FEATURE [PartDesign::Body] PocketBody  label="Tail_Vane_Bracket_Body"
  Group = -> [Sketch,Pad,Sketch001,Pocket]
  Openafpm_Flat = true
  Origin = -> Origin001
  Tip = -> Pocket
FEATURE [App::Link] Link  label="Bolt"
  LinkPlacement = pos=(0,0,5) rot=(0,0,1;0rad)
  LinkedObject = -> <external ../../Fasteners/Fastener_Bolt_Tail_Vane.FCStd>#Body
  Placement = pos=(0,0,5) rot=(0,0,1;0rad)
  expr: .Placement.Base.z = Spreadsheet.BoltZ
FEATURE [App::Link] Link002  label="HexNut"
  LinkPlacement = pos=(0,0,-18.69) rot=(0,0,1;0rad)
  LinkedObject = -> <external ../../Fasteners/Fastener_HexNut.FCStd>#Body
  Placement = pos=(0,0,-18.69) rot=(0,0,1;0rad)
  expr: .Placement.Base.z = Spreadsheet.HexNutZ
FEATURE [App::Link] Link003  label="Assembly_BoltNut_Second"
  LinkPlacement = pos=(180,15,0) rot=(0,0,1;0rad)
  LinkedObject = -> Part001
  Placement = pos=(180,15,0) rot=(0,0,1;0rad)
  expr: .Placement.Base.x = Spreadsheet.DistanceToSecondHole
  expr: .Placement.Base.y = Spreadsheet.Y_Holes
FEATURE [App::Link] Link004  label="Washer"
  LinkPlacement = pos=(0,0,-8.5) rot=(0,0,1;0rad)
  LinkedObject = -> <external ../../Fasteners/Fastener_Washer_Wide.FCStd>#Tube
  Placement = pos=(0,0,-8.5) rot=(0,0,1;0rad)
  expr: .Placement.Base.z = Spreadsheet.WasherZ
FEATURE [App::Part] Part001  label="Assembly_BoltNut_First"
  Group = -> [Link,Link002,Link004]
  Origin = -> Origin002
  Placement = pos=(30,15,0) rot=(0,0,1;0rad)
  expr: .Placement.Base.x = Spreadsheet.DistanceToFirstHole
  expr: .Placement.Base.y = Spreadsheet.Y_Holes
FEATURE [App::Part] Part  label="Tail_Vane_Bracket"
  Group = -> [PocketBody,Part001,Link003]
  Origin = -> Origin
  Placement = pos=(0,0,0) rot=(0.57735,-0.57735,-0.57735;4.18879rad)
